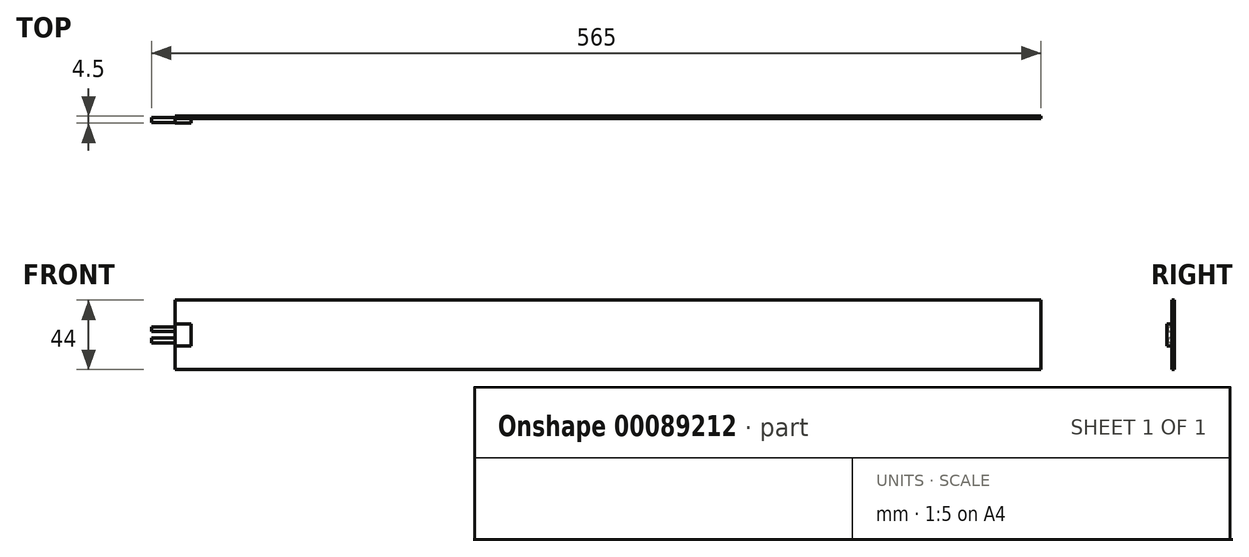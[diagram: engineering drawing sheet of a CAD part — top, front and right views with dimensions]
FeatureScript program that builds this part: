
annotation { "Feature Type Name" : "Feature", "Feature Type Description" : "" }
export const myFeature = defineFeature(function(context is Context, id is Id, definition is map)
    precondition{}
    {
        {
            var Q0;
            Q0=qCreatedBy(makeId("Front.planeOp"),FACE);
            var sketch = newSketch(context, id + "F0", { "sketchPlane" : qUnion([Q0])});
            skLineSegment(sketch, "E0.bottom", {"start": v(0, 0) * mm, "end": v(550, 0) * mm});
            skLineSegment(sketch, "E0.top", {"start": v(0, 44) * mm, "end": v(550, 44) * mm});
            skLineSegment(sketch, "E0.left", {"start": v(0, 0) * mm, "end": v(0, 44) * mm});
            skLineSegment(sketch, "E0.right", {"start": v(550, 0) * mm, "end": v(550, 44) * mm});
            skSolve(sketch);
        }
        {
            var Q0;
            Q0=makeQuery(id+"F0.imprint","IMPRINT",FACE,{"disambiguationData":[TD([[makeQuery(id+"F0.imprint","IMPRINT",EDGE,{"derivedFrom":sQuery(id+"F0.wireOp",EDGE,"E0.bottom")}),1.0]])]});
            extrude(context, id + "F1", {"entities" : qUnion([Q0]), "depth" : 1.5 * mm});
        }
        {
            var Q0;
            Q0=makeQuery(id+"F1.opExtrude","CAP_FACE",FACE,{"disambiguationData":[OSD([sQuery(id+"F0.wireOp",EDGE,"E0.bottom"),sQuery(id+"F0.wireOp",EDGE,"E0.top"),sQuery(id+"F0.wireOp",EDGE,"E0.left"),sQuery(id+"F0.wireOp",EDGE,"E0.right")])],"isStart":false});
            var sketch = newSketch(context, id + "F2", { "sketchPlane" : qUnion([Q0])});
            skLineSegment(sketch, "E1.bottom", {"start": v(0, 29) * mm, "end": v(10, 29) * mm});
            skLineSegment(sketch, "E1.top", {"start": v(0, 15) * mm, "end": v(10, 15) * mm});
            skLineSegment(sketch, "E1.left", {"start": v(0, 29) * mm, "end": v(0, 15) * mm});
            skLineSegment(sketch, "E1.right", {"start": v(10, 29) * mm, "end": v(10, 15) * mm});
            skSolve(sketch);
        }
        {
            var Q0;
            Q0 = qSketchRegion(id + "F2", true);
            extrude(context, id + "F3", {"entities" : qUnion([Q0]), "operationType" : NewBodyOperationType.ADD, "depth" : 3 * mm});
        }
        {
            var Q0;
            Q0=makeQuery(id+"F3.boolean.opBoolean","MERGE",FACE,{"derivedFrom":[makeQuery(id+"F1.opExtrude","SWEPT_FACE",FACE,{"disambiguationData":[OSD([sQuery(id+"F0.wireOp",EDGE,"E0.left")])]}),makeQuery(id+"F3.opExtrude","SWEPT_FACE",FACE,{"disambiguationData":[OSD([sQuery(id+"F2.wireOp",EDGE,"E1.left")])]})]});
            var sketch = newSketch(context, id + "F4", { "sketchPlane" : qUnion([Q0])});
            skCircle(sketch, "E2", {"center": v(2.5, 25.5) * mm, "radius": 1.5 * mm});
            skCircle(sketch, "E3", {"center": v(2.5, 18.5) * mm, "radius": 1.5 * mm});
            skSolve(sketch);
        }
        {
            var Q0;
            Q0 = qSketchRegion(id + "F4", true);
            extrude(context, id + "F5", {"entities" : qUnion([Q0]), "operationType" : NewBodyOperationType.ADD, "depth" : 15 * mm});
        }
    });
